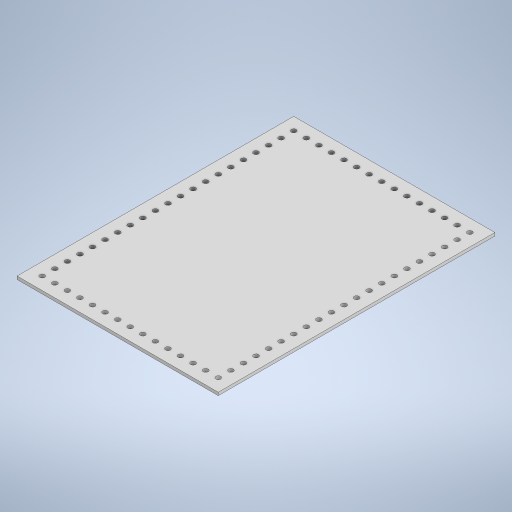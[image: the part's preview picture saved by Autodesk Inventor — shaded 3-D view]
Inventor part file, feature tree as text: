
AUTODESK INVENTOR PART (.ipt)
format: ipt  version: 2023.4 (Build 274418000, 418)  size: 339,968 bytes
history: native  units: in
note: dims shown in document units (in); Inventor stores cm internally (conversion verified against a paired STEP export)
features: sketch x2, sheet_metal_op x1, extrude x1, other x1
ambient origin geometry x8: Origin, YZ Plane, XZ Plane, XY Plane, X Axis, Y Axis, Z Axis, Center Point
bodies: Solid1 (feature_tree)
feature tree (5):
  sheet_metal_op  "Face1"
  extrude  "Extrusion1"  Depth=11.0in
  sketch  "Sketch1"  dims[d0=8.0in d1=11.0in]
  other  "Plate1"
  sketch  "Sketch2"  dims[d2=0.12in d3=0.197in d4=0.5in d5=0.5in d6=5.5118in d8=0.5in d9=0.3937in d11=1.0in d13=0.197in d15=0.5in d16=0.5in d17=7.874in d19=0.5in d20=0.3937in d22=1.0in d24=0.197in d25=0.5in d26=0.5in d27=5.5118in d29=0.5in d30=0.3937in d32=1.0in d34=0.197in d35=0.5in d36=0.5in d37=7.874in d39=0.5in d40=0.3937in d42=1.0in d44=1.0in d45=0.0in]
